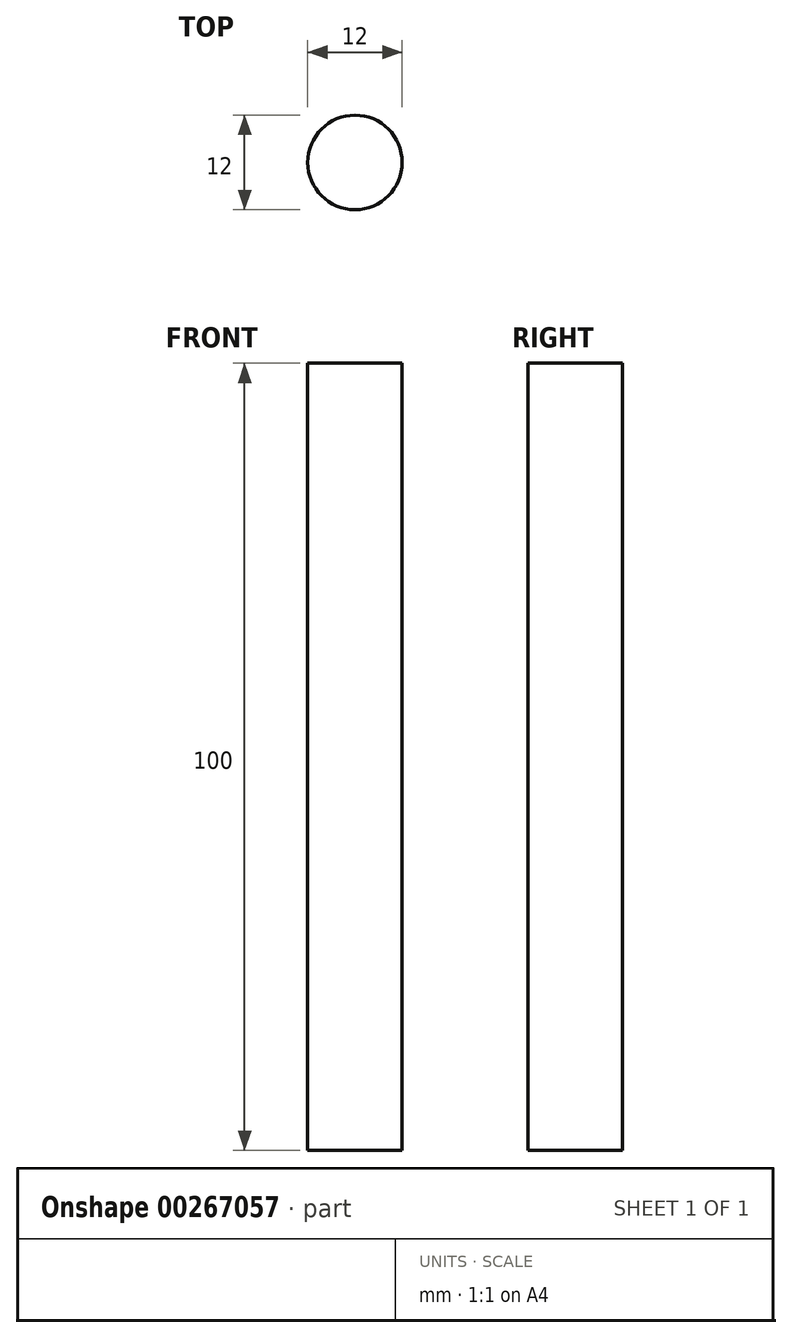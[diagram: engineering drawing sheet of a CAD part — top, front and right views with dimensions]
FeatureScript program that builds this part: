
annotation { "Feature Type Name" : "Feature", "Feature Type Description" : "" }
export const myFeature = defineFeature(function(context is Context, id is Id, definition is map)
    precondition{}
    {
        {
            var Q0;
            Q0=qCreatedBy(makeId("Top.planeOp"),FACE);
            var sketch = newSketch(context, id + "F0", { "sketchPlane" : qUnion([Q0])});
            skCircle(sketch, "E0", {"center": v(0, 0) * mm, "radius": 6 * mm});
            skSolve(sketch);
        }
        {
            var Q0;
            Q0 = qSketchRegion(id + "F0", true);
            extrude(context, id + "F1", {"entities" : qUnion([Q0]), "depth" : 100 * mm, "offsetDistance" : 25 * mm});
        }
    });
